# Revit family: Konsole 35- 21 Platte längs, VA
name_source: partatom
category: HLS-Bauteile
revit_build: Autodesk Revit 2017 (Build: 20190507_1515(x64)
units: mm (PartAtom-declared; Revit-internal decimal feet)

## family parameters
Basisbauteil = Fläche
Beim Laden mit Abzugskörper schneiden = Nein
Bemaßung runder Anschluss = Durchmesser verwenden
Gemeinsam genutzt = Ja
Raumberechnungspunkt = Nein
Teiletyp = Normal

## types (6) — shared parameters
Ausrichtung Platte = längs
Breite Platte = 40 mm  [stored 0.131234 ft]
Breite Profil = 35 mm  [stored 0.114829 ft]
Fabrikat = MEFA
Firma = MEFA Befestigungs- und Montagesysteme GmbH
Höhe Profil = 21 mm  [stored 0.0688976 ft]
Lochabstand = 90 mm
Länge Platte = 120 mm  [stored 0.393701 ft]
Material = Edelstahl
Profil = C-Profil
Stärke Platte = 5 mm  [stored 0.0164042 ft]
Stärke Profil = 2 mm  [stored 0.00656168 ft]
Vorgabe-Ansicht = 1219 mm

## per-type parameters (varying)
| type | Artikelnummer | EAN | Gewicht | Gewicht pro Bauteil | Kurztext1 | Kurztext2 | Länge Konsole | Materialname C-Profil | Materialname Platte | Schienenlänge | max. zul. Last F1 | max. zul. Last F2 | max. zul. Last q0 |
| Konsole 35- 21 L= 420 Platte längs V4A | 0584021 | 4250928414915 | 0.69 kg | 0.69 kg | Konsole C-Profil 35/21 V4A | L= 420 mm Platte längs | 420 mm  [stored 1.37795 ft] | 1.4571 | 1.4571 | Montageschiene 35- 21-2,0 für Konsole VA : C-Profil 35- 21-2,0 L=  420 V4A | 0.08 kip | 0.04 kip | 0.060 kip/ft |
| Konsole 35- 21 L= 420 Platte längs V2A | 0584020 | 4250928414908 | 0.69 kg | 0.69 kg | Konsole C-Profil 35/21 V2A | L= 420 mm Platte längs | 420 mm  [stored 1.37795 ft] | 1.4301 | 1.4301 | Montageschiene 35- 21-2,0 für Konsole VA : C-Profil 35- 21-2,0 L=  420 V2A | 0.07 kip | 0.03 kip | 0.050 kip/ft |
| Konsole 35- 21 L= 315 Platte längs V4A | 0583021 | 4250928414892 | 0.56 kg | 0.56 kg | Konsole C-Profil 35/21 V4A | L= 315 mm Platte längs | 315 mm  [stored 1.03346 ft] | 1.4571 | 1.4571 | Montageschiene 35- 21-2,0 für Konsole VA : C-Profil 35- 21-2,0 L=  315 V4A | 0.11 kip | 0.06 kip | 0.107 kip/ft |
| Konsole 35- 21 L= 315 Platte längs V2A | 0583020 | 4250928414885 | 0.57 kg | 0.57 kg | Konsole C-Profil 35/21 V2A | L= 315 mm Platte längs | 315 mm  [stored 1.03346 ft] | 1.4301 | 1.4301 | Montageschiene 35- 21-2,0 für Konsole VA : C-Profil 35- 21-2,0 L=  315 V2A | 0.09 kip | 0.04 kip | 0.089 kip/ft |
| Konsole 35- 21 L= 262,5 Platte längs, V4A | 0582021 | 4250928414878 | 0.51 kg | 0.51 kg | Konsole C-Profil 35/21 V4A | L= 262,5 mm Platte längs | 263 mm | 1.4571 | 1.4571 | Montageschiene 35- 21-2,0 für Konsole VA : C-Profil 35- 21-2,0 L=  262,5 V4A | 0.13 kip | 0.09 kip | 0.153 kip/ft |
| Konsole 35- 21 L= 262,5 Platte längs, V2A | 0582020 | 4250928414861 | 0.51 kg | 0.51 kg | Konsole C-Profil 35/21 V2A | L= 262,5 mm Platte längs | 263 mm | 1.4301 | 1.4301 | Montageschiene 35- 21-2,0 für Konsole VA : C-Profil 35- 21-2,0 L=  262,5 V2A | 0.11 kip | 0.06 kip | 0.128 kip/ft |

note: [stored X ft] marks values corroborated as IEEE doubles in the binary element streams (Revit-internal decimal feet)
